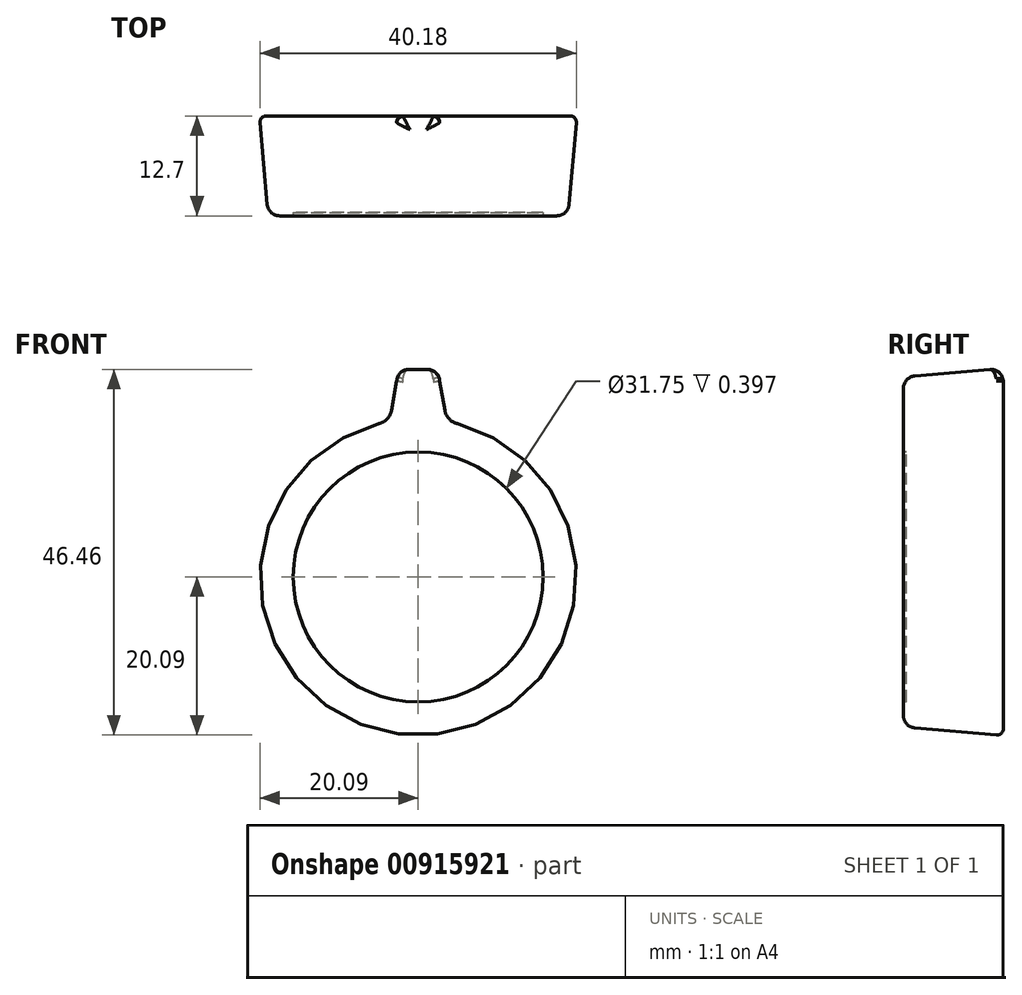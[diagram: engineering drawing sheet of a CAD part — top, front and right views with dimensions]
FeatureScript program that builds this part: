
annotation { "Feature Type Name" : "Feature", "Feature Type Description" : "" }
export const myFeature = defineFeature(function(context is Context, id is Id, definition is map)
    precondition{}
    {
        {
            var Q0;
            Q0=qCreatedBy(makeId("Front.planeOp"),FACE);
            var sketch = newSketch(context, id + "F0", { "sketchPlane" : qUnion([Q0])});
            skArc(sketch, "E0", {"start": v(-4.7, 18.46) * mm, "mid": v(2.37, -18.9) * mm, "end": v(0, 19.05) * mm});
            skLineSegment(sketch, "E1", {"start": v(-1.59, 25.4) * mm, "end": v(0, 25.4) * mm});
            skLineSegment(sketch, "E2", {"start": v(0, 19.05) * mm, "end": v(0, 25.4) * mm, "construction": true});
            skLineSegment(sketch, "E3", {"start": v(-1.59, 25.4) * mm, "end": v(-2.37, 20.98) * mm});
            skPoint(sketch, "E4.visualSharp", {"position": v(-2.74, 18.85) * mm});
            skArc(sketch, "E4.filletArc", {"start": v(-4.7, 18.46) * mm, "mid": v(-3.17, 19.38) * mm, "end": v(-2.37, 20.98) * mm});
            skLineSegment(sketch, "E5.MirrorCS", {"start": v(1.59, 25.4) * mm, "end": v(0, 25.4) * mm});
            skLineSegment(sketch, "E6.MirrorCS", {"start": v(1.59, 25.4) * mm, "end": v(2.37, 20.98) * mm});
            skArc(sketch, "E7.MirrorCS", {"start": v(4.7, 18.46) * mm, "mid": v(3.17, 19.38) * mm, "end": v(2.37, 20.98) * mm});
            skSolve(sketch);
        }
        {
            var Q0;
            Q0 = qSketchRegion(id + "F0", true);
            extrude(context, id + "F1", {"entities" : qUnion([Q0]), "oppositeDirection" : true, "depth" : 12.7 * mm, "offsetDistance" : 25.4 * mm, "hasDraft" : true, "draftAngle" : 5 * degree});
        }
        {
            var Q0;
            Q0=makeQuery(id+"F1.opExtrude","CAP_EDGE",EDGE,{"disambiguationData":[OSD([sQuery(id+"F0.wireOp",EDGE,"E0")])],"isStart":false});
            fillet(context, id + "F2", {"entities" : qUnion([Q0]), "radius" : 0.8 * mm, "tangentPropagation" : true, "allowEdgeOverflow" : false});
        }
        {
            var Q0;
            Q0=makeQuery(id+"F1.opExtrude","CAP_EDGE",EDGE,{"disambiguationData":[OSD([sQuery(id+"F0.wireOp",EDGE,"E0")])],"isStart":true});
            var Q1;
            Q1=makeQuery(id+"F1.opExtrude","SWEPT_EDGE",EDGE,{"disambiguationData":[OSD([sQuery(id+"F0.wireOp",EDGE,"E5.MirrorCS"),sQuery(id+"F0.wireOp",EDGE,"E6.MirrorCS")])]});
            var Q2;
            Q2=makeQuery(id+"F1.opExtrude","CAP_EDGE",EDGE,{"disambiguationData":[OSD([sQuery(id+"F0.wireOp",EDGE,"E1"),sQuery(id+"F0.wireOp",EDGE,"E5.MirrorCS")])],"isStart":true});
            fillet(context, id + "F3", {"entities" : qUnion([Q0, Q1, Q2]), "radius" : 1.59 * mm, "tangentPropagation" : true, "allowEdgeOverflow" : false});
        }
        {
            var Q0;
            Q0=makeQuery(id+"F1.opExtrude","CAP_FACE",FACE,{"disambiguationData":[OSD([sQuery(id+"F0.wireOp",EDGE,"E0"),sQuery(id+"F0.wireOp",EDGE,"E1"),sQuery(id+"F0.wireOp",EDGE,"E3"),sQuery(id+"F0.wireOp",EDGE,"E4.filletArc"),sQuery(id+"F0.wireOp",EDGE,"E5.MirrorCS"),sQuery(id+"F0.wireOp",EDGE,"E6.MirrorCS"),sQuery(id+"F0.wireOp",EDGE,"E7.MirrorCS")])],"isStart":true});
            var sketch = newSketch(context, id + "F4", { "sketchPlane" : qUnion([Q0])});
            skCircle(sketch, "E8", {"center": v(0, 0) * mm, "radius": 15.88 * mm});
            skSolve(sketch);
        }
        {
            var Q0;
            Q0 = qSketchRegion(id + "F4", true);
            extrude(context, id + "F5", {"entities" : qUnion([Q0]), "operationType" : NewBodyOperationType.REMOVE, "oppositeDirection" : true, "depth" : 0.4 * mm, "offsetDistance" : 25.4 * mm});
        }
    });
